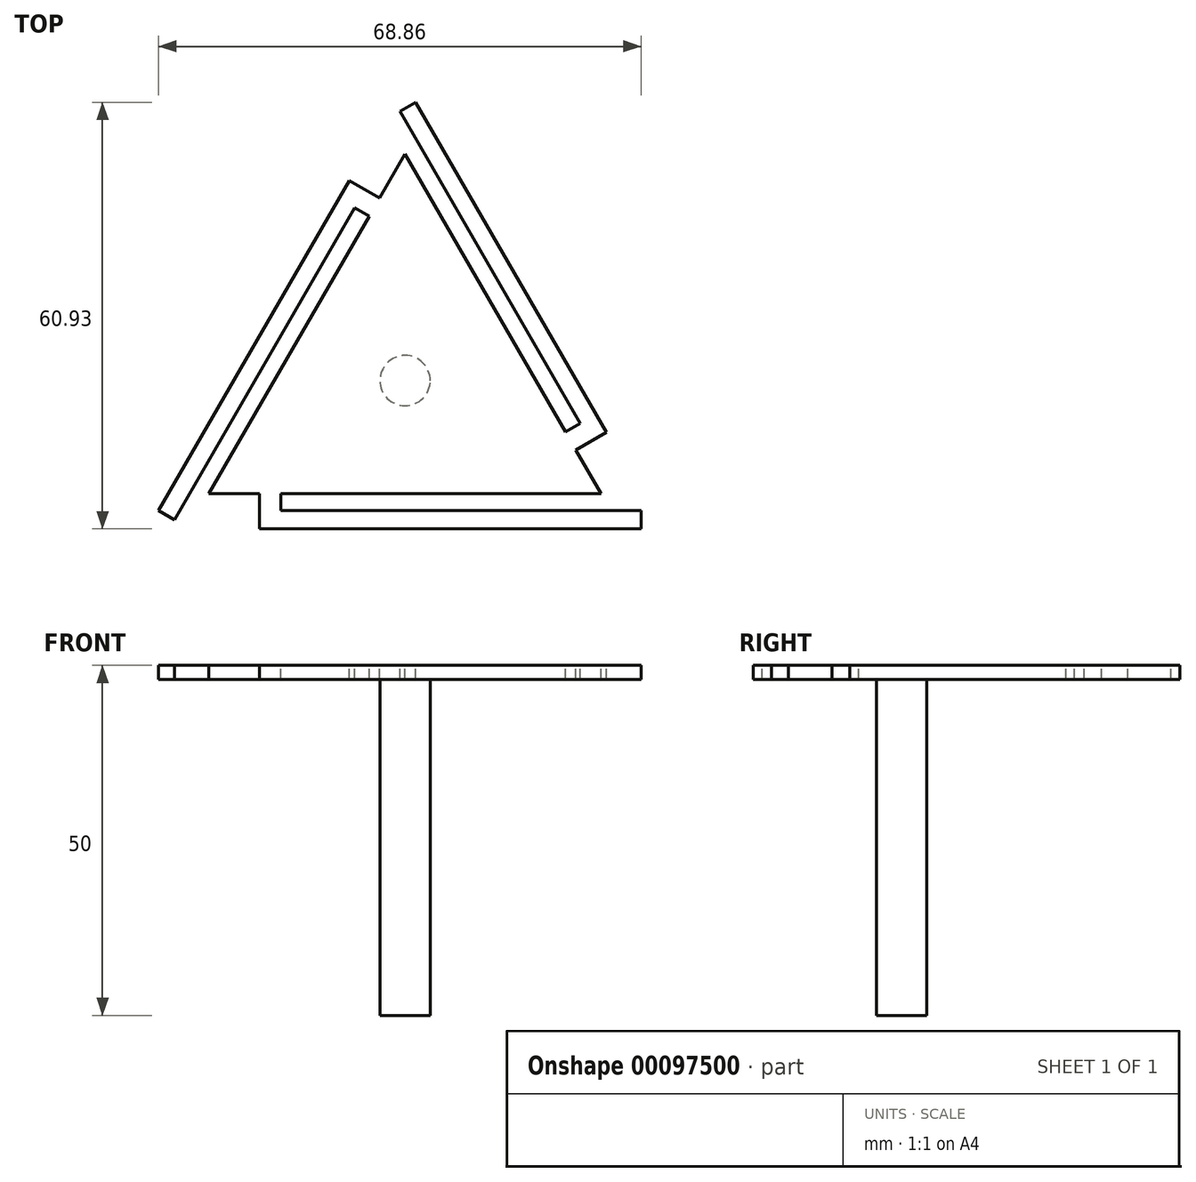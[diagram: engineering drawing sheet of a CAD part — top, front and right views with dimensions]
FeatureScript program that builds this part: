
annotation { "Feature Type Name" : "Feature", "Feature Type Description" : "" }
export const myFeature = defineFeature(function(context is Context, id is Id, definition is map)
    precondition{}
    {
        {
            var Q0;
            Q0=qCreatedBy(makeId("Top.planeOp"),FACE);
            var sketch = newSketch(context, id + "F0", { "sketchPlane" : qUnion([Q0])});
            skLineSegment(sketch, "E0", {"start": v(0, 48.5) * mm, "end": v(-1.5, 45.9) * mm});
            skLineSegment(sketch, "E1", {"start": v(-28, 0) * mm, "end": v(-25, 0) * mm});
            skLineSegment(sketch, "E2", {"start": v(28, 0) * mm, "end": v(26.5, 2.6) * mm});
            skLineSegment(sketch, "E3", {"start": v(-1.5, 45.9) * mm, "end": v(-26.5, 2.6) * mm});
            skLineSegment(sketch, "E4", {"start": v(1.5, 45.9) * mm, "end": v(0, 48.5) * mm});
            skLineSegment(sketch, "E5", {"start": v(-26.5, 2.6) * mm, "end": v(-28, 0) * mm});
            skLineSegment(sketch, "E6", {"start": v(-25, 0) * mm, "end": v(25, 0) * mm});
            skLineSegment(sketch, "E7", {"start": v(25, 0) * mm, "end": v(28, 0) * mm});
            skLineSegment(sketch, "E8", {"start": v(26.5, 2.6) * mm, "end": v(1.5, 45.9) * mm});
            skLineSegment(sketch, "E9", {"start": v(-26.5, 2.6) * mm, "end": v(-25, 0) * mm});
            skLineSegment(sketch, "E10", {"start": v(25, 0) * mm, "end": v(26.5, 2.6) * mm});
            skLineSegment(sketch, "E11", {"start": v(-35.18, -2.41) * mm, "end": v(-7.96, 44.74) * mm});
            skLineSegment(sketch, "E12", {"start": v(-3.62, 42.23) * mm, "end": v(-7.96, 44.74) * mm});
            skLineSegment(sketch, "E13", {"start": v(1.5, 55.92) * mm, "end": v(28.72, 8.77) * mm});
            skLineSegment(sketch, "E14", {"start": v(28.72, 8.77) * mm, "end": v(24.38, 6.27) * mm});
            skLineSegment(sketch, "E15", {"start": v(33.68, -5) * mm, "end": v(-20.76, -5) * mm});
            skLineSegment(sketch, "E16", {"start": v(-20.76, -2.41) * mm, "end": v(-20.76, 0) * mm});
            skLineSegment(sketch, "E17", {"start": v(-9.46, 42.14) * mm, "end": v(-5.12, 39.63) * mm});
            skLineSegment(sketch, "E18", {"start": v(27.22, 11.37) * mm, "end": v(22.88, 8.86) * mm});
            skLineSegment(sketch, "E19", {"start": v(-20.76, -5) * mm, "end": v(-20.76, -2.41) * mm});
            skLineSegment(sketch, "E20", {"start": v(-17.76, -5) * mm, "end": v(-17.76, 0) * mm});
            skLineSegment(sketch, "E21", {"start": v(-35.18, -2.41) * mm, "end": v(-32.93, -3.71) * mm});
            skPoint(sketch, "E21.endSnap0", {"position": v(-34.43, -3.71) * mm});
            skLineSegment(sketch, "E22", {"start": v(33.68, -5) * mm, "end": v(33.68, -2.41) * mm});
            skLineSegment(sketch, "E23", {"start": v(1.5, 55.92) * mm, "end": v(-0.75, 54.62) * mm});
            skLineSegment(sketch, "E24", {"start": v(-0.75, 54.62) * mm, "end": v(26.47, 7.47) * mm});
            skLineSegment(sketch, "E25", {"start": v(-32.93, -3.71) * mm, "end": v(-5.7, 43.44) * mm});
            skLineSegment(sketch, "E26", {"start": v(33.68, -2.41) * mm, "end": v(-20.76, -2.41) * mm});
            skPoint(sketch, "E27.orphan", {"position": v(-33.68, -5) * mm});
            skPoint(sketch, "E28.end.orphan", {"position": v(-1.5, 55.92) * mm});
            skLineSegment(sketch, "E29", {"start": v(-14, 24.25) * mm, "end": v(0, 16.17) * mm});
            skLineSegment(sketch, "E30", {"start": v(0, 16.17) * mm, "end": v(14, 24.25) * mm});
            skCircle(sketch, "E31", {"center": v(0, 16.17) * mm, "radius": 13.77 * mm});
            skCircle(sketch, "E32", {"center": v(0, 16.17) * mm, "radius": 3.6 * mm});
            skSolve(sketch);
        }
        {
            var Q0;
            {var subQ0=sQuery(id+"F0.wireOp",EDGE,"E21");Q0=makeQuery(id+"F0.imprint","IMPRINT",FACE,{"disambiguationData":[TD([[makeQuery(id+"F0.imprint","IMPRINT",EDGE,{"derivedFrom":subQ0}),1.0]])]});}
            var Q1;
            {var subQ0=sQuery(id+"F0.wireOp",EDGE,"E22");Q1=makeQuery(id+"F0.imprint","IMPRINT",FACE,{"disambiguationData":[TD([[makeQuery(id+"F0.imprint","IMPRINT",EDGE,{"derivedFrom":subQ0}),1.0]])]});}
            var Q2;
            {var subQ13=sQuery(id+"F0.wireOp",EDGE,"E9");Q2=makeQuery(id+"F0.imprint","IMPRINT",FACE,{"disambiguationData":[TD([[makeQuery(id+"F0.imprint","IMPRINT",EDGE,{"derivedFrom":subQ13}),1.0]])]});}
            var Q3;
            {var subQ9=sQuery(id+"F0.wireOp",EDGE,"E0");Q3=makeQuery(id+"F0.imprint","IMPRINT",FACE,{"disambiguationData":[TD([[makeQuery(id+"F0.imprint","IMPRINT",EDGE,{"derivedFrom":subQ9}),1.0]])]});}
            var Q4;
            {var subQ0=sQuery(id+"F0.wireOp",EDGE,"E23");Q4=makeQuery(id+"F0.imprint","IMPRINT",FACE,{"disambiguationData":[TD([[makeQuery(id+"F0.imprint","IMPRINT",EDGE,{"derivedFrom":subQ0}),1.0]])]});}
            var Q5;
            Q5=makeQuery(id+"F0.imprint","IMPRINT",FACE,{"disambiguationData":[TD([[makeQuery(id+"F0.imprint","IMPRINT",EDGE,{"derivedFrom":sQuery(id+"F0.wireOp",EDGE,"E1")}),1.0]])]});
            var Q6;
            {var subQ0=sQuery(id+"F0.wireOp",EDGE,"E12");var subQ1=sQuery(id+"F0.wireOp",EDGE,"E3");var subQ2=makeQuery(id+"F0.imprint","INTERSECT",VERTEX,{"derivedFrom":[subQ1,subQ0]});Q6=makeQuery(id+"F0.imprint","IMPRINT",FACE,{"disambiguationData":[TD([[makeQuery(id+"F0.imprint","IMPRINT",EDGE,{"disambiguationData":[TD([[subQ2,-1.0]])],"derivedFrom":subQ1}),-1.0]])]});}
            var Q7;
            {var subQ0=sQuery(id+"F0.wireOp",EDGE,"E30");var subQ1=sQuery(id+"F0.wireOp",EDGE,"E29");var subQ2=makeQuery(id+"F0.imprint","INTERSECT",VERTEX,{"derivedFrom":[subQ1,subQ0]});Q7=makeQuery(id+"F0.imprint","IMPRINT",FACE,{"disambiguationData":[TD([[makeQuery(id+"F0.imprint","IMPRINT",EDGE,{"disambiguationData":[TD([[subQ2,1.0]])],"derivedFrom":subQ1}),-1.0]])]});}
            var Q8;
            {var subQ0=sQuery(id+"F0.wireOp",EDGE,"E14");var subQ1=sQuery(id+"F0.wireOp",EDGE,"E8");var subQ2=makeQuery(id+"F0.imprint","INTERSECT",VERTEX,{"derivedFrom":[subQ1,subQ0]});Q8=makeQuery(id+"F0.imprint","IMPRINT",FACE,{"disambiguationData":[TD([[makeQuery(id+"F0.imprint","IMPRINT",EDGE,{"disambiguationData":[TD([[subQ2,-1.0]])],"derivedFrom":subQ1}),-1.0]])]});}
            var Q9;
            {var subQ0=sQuery(id+"F0.wireOp",EDGE,"E16");Q9=makeQuery(id+"F0.imprint","IMPRINT",FACE,{"disambiguationData":[TD([[makeQuery(id+"F0.imprint","IMPRINT",EDGE,{"derivedFrom":subQ0}),-1.0]])]});}
            var Q10;
            {var subQ0=sQuery(id+"F0.wireOp",EDGE,"E12");var subQ1=sQuery(id+"F0.wireOp",EDGE,"E11");var subQ2=makeQuery(id+"F0.imprint","INTERSECT",VERTEX,{"derivedFrom":[subQ1,subQ0]});Q10=makeQuery(id+"F0.imprint","IMPRINT",FACE,{"disambiguationData":[TD([[makeQuery(id+"F0.imprint","IMPRINT",EDGE,{"disambiguationData":[TD([[subQ2,1.0]])],"derivedFrom":subQ1}),-1.0]])]});}
            var Q11;
            {var subQ0=sQuery(id+"F0.wireOp",EDGE,"E14");var subQ1=sQuery(id+"F0.wireOp",EDGE,"E13");var subQ2=makeQuery(id+"F0.imprint","INTERSECT",VERTEX,{"derivedFrom":[subQ1,subQ0]});Q11=makeQuery(id+"F0.imprint","IMPRINT",FACE,{"disambiguationData":[TD([[makeQuery(id+"F0.imprint","IMPRINT",EDGE,{"disambiguationData":[TD([[subQ2,1.0]])],"derivedFrom":subQ1}),-1.0]])]});}
            var Q12;
            {var subQ0=sQuery(id+"F0.wireOp",EDGE,"E30");var subQ1=sQuery(id+"F0.wireOp",EDGE,"E29");var subQ2=makeQuery(id+"F0.imprint","INTERSECT",VERTEX,{"derivedFrom":[subQ1,subQ0]});Q12=makeQuery(id+"F0.imprint","IMPRINT",FACE,{"disambiguationData":[TD([[makeQuery(id+"F0.imprint","IMPRINT",EDGE,{"disambiguationData":[TD([[subQ2,1.0]])],"derivedFrom":subQ1}),1.0]])]});}
            var Q13;
            {var subQ0=sQuery(id+"F0.wireOp",EDGE,"E19");Q13=makeQuery(id+"F0.imprint","IMPRINT",FACE,{"disambiguationData":[TD([[makeQuery(id+"F0.imprint","IMPRINT",EDGE,{"derivedFrom":subQ0}),-1.0]])]});}
            var Q14;
            Q14=makeQuery(id+"F0.imprint","IMPRINT",FACE,{"disambiguationData":[TD([[makeQuery(id+"F0.imprint","IMPRINT",EDGE,{"derivedFrom":sQuery(id+"F0.wireOp",EDGE,"E2")}),1.0]])]});
            var Q15;
            {var subQ0=sQuery(id+"F0.wireOp",EDGE,"E31");var subQ1=sQuery(id+"F0.wireOp",EDGE,"E29");var subQ2=makeQuery(id+"F0.imprint","INTERSECT",VERTEX,{"derivedFrom":[subQ1,subQ0]});Q15=makeQuery(id+"F0.imprint","IMPRINT",FACE,{"disambiguationData":[TD([[makeQuery(id+"F0.imprint","IMPRINT",EDGE,{"disambiguationData":[TD([[subQ2,-1.0]])],"derivedFrom":subQ1}),1.0]])]});}
            var Q16;
            {var subQ0=sQuery(id+"F0.wireOp",EDGE,"E31");var subQ1=sQuery(id+"F0.wireOp",EDGE,"E29");var subQ2=makeQuery(id+"F0.imprint","INTERSECT",VERTEX,{"derivedFrom":[subQ1,subQ0]});Q16=makeQuery(id+"F0.imprint","IMPRINT",FACE,{"disambiguationData":[TD([[makeQuery(id+"F0.imprint","IMPRINT",EDGE,{"disambiguationData":[TD([[subQ2,-1.0]])],"derivedFrom":subQ1}),-1.0]])]});}
            extrude(context, id + "F1", {"entities" : qUnion([Q0, Q1, Q2, Q3, Q4, Q5, Q6, Q7, Q8, Q9, Q10, Q11, Q12, Q13, Q14, Q15, Q16]), "oppositeDirection" : true, "depth" : 2 * mm});
        }
        {
            var Q0;
            {var subQ0=sQuery(id+"F0.wireOp",EDGE,"E30");var subQ1=sQuery(id+"F0.wireOp",EDGE,"E29");var subQ2=makeQuery(id+"F0.imprint","INTERSECT",VERTEX,{"derivedFrom":[subQ1,subQ0]});Q0=makeQuery(id+"F0.imprint","IMPRINT",FACE,{"disambiguationData":[TD([[makeQuery(id+"F0.imprint","IMPRINT",EDGE,{"disambiguationData":[TD([[subQ2,1.0]])],"derivedFrom":subQ1}),-1.0]])]});}
            var Q1;
            {var subQ0=sQuery(id+"F0.wireOp",EDGE,"E30");var subQ1=sQuery(id+"F0.wireOp",EDGE,"E29");var subQ2=makeQuery(id+"F0.imprint","INTERSECT",VERTEX,{"derivedFrom":[subQ1,subQ0]});Q1=makeQuery(id+"F0.imprint","IMPRINT",FACE,{"disambiguationData":[TD([[makeQuery(id+"F0.imprint","IMPRINT",EDGE,{"disambiguationData":[TD([[subQ2,1.0]])],"derivedFrom":subQ1}),1.0]])]});}
            extrude(context, id + "F2", {"entities" : qUnion([Q0, Q1]), "operationType" : NewBodyOperationType.ADD, "oppositeDirection" : true, "depth" : 50 * mm});
        }
    });
